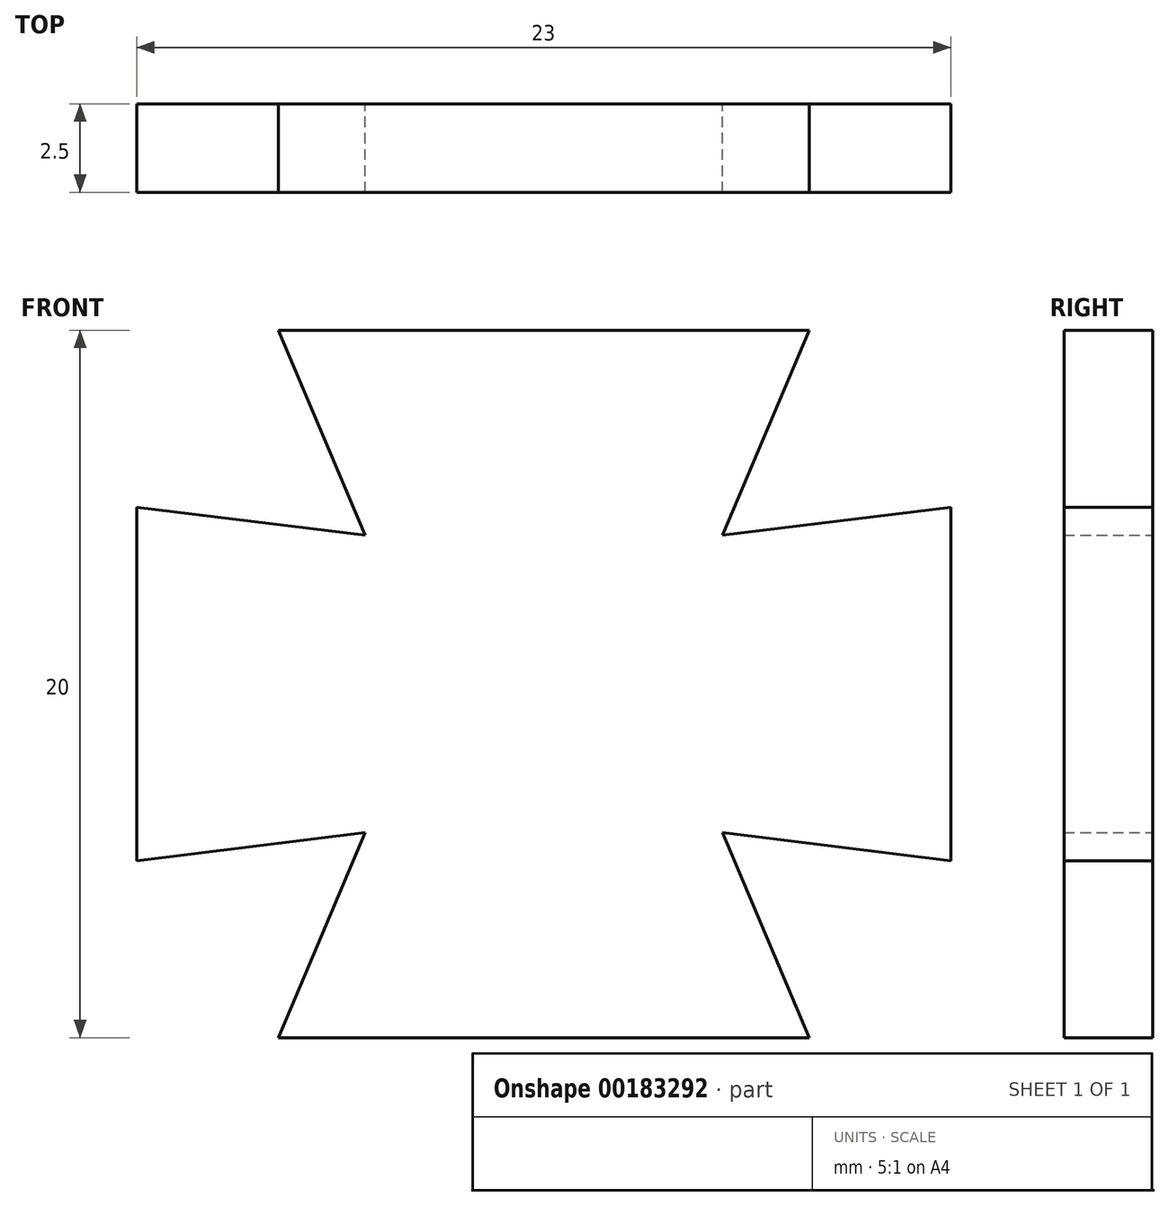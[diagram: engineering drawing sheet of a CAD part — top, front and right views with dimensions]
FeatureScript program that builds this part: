
annotation { "Feature Type Name" : "Feature", "Feature Type Description" : "" }
export const myFeature = defineFeature(function(context is Context, id is Id, definition is map)
    precondition{}
    {
        {
            var Q0;
            Q0=qCreatedBy(makeId("Front.planeOp"),FACE);
            var sketch = newSketch(context, id + "F0", { "sketchPlane" : qUnion([Q0])});
            skLineSegment(sketch, "E0", {"start": v(0, 0) * mm, "end": v(-11.5, 0) * mm});
            skLineSegment(sketch, "E1", {"start": v(0, 0) * mm, "end": v(0, 10) * mm});
            skLineSegment(sketch, "E2", {"start": v(0, 0) * mm, "end": v(0, -10) * mm});
            skLineSegment(sketch, "E3", {"start": v(0, -10) * mm, "end": v(-7.5, -10) * mm});
            skLineSegment(sketch, "E4", {"start": v(-7.5, -10) * mm, "end": v(-5.05, -4.2) * mm});
            skLineSegment(sketch, "E5", {"start": v(-5.05, -4.2) * mm, "end": v(-11.5, -5) * mm});
            skLineSegment(sketch, "E6", {"start": v(-11.5, -5) * mm, "end": v(-11.5, 0) * mm});
            skLineSegment(sketch, "E7", {"start": v(-11.5, 0) * mm, "end": v(-11.5, 5) * mm});
            skLineSegment(sketch, "E8", {"start": v(-11.5, 5) * mm, "end": v(-5.05, 4.2) * mm});
            skLineSegment(sketch, "E9", {"start": v(-5.05, 4.2) * mm, "end": v(-7.5, 10) * mm});
            skLineSegment(sketch, "E10", {"start": v(-7.5, 10) * mm, "end": v(0, 10) * mm});
            skLineSegment(sketch, "E11", {"start": v(0, 10) * mm, "end": v(0, -10) * mm});
            skLineSegment(sketch, "E12", {"start": v(0, 14.62) * mm, "end": v(0, -19.55) * mm});
            skPoint(sketch, "E12.endSnap0", {"position": v(0, -5) * mm});
            skSolve(sketch);
        }
        {
            var Q0;
            {var subQ0=sQuery(id+"F0.wireOp",EDGE,"E0");Q0=makeQuery(id+"F0.imprint","IMPRINT",FACE,{"disambiguationData":[TD([[makeQuery(id+"F0.imprint","IMPRINT",EDGE,{"derivedFrom":subQ0}),-1.0]])]});}
            var Q1;
            {var subQ1=sQuery(id+"F0.wireOp",EDGE,"E0");Q1=makeQuery(id+"F0.imprint","IMPRINT",FACE,{"disambiguationData":[TD([[makeQuery(id+"F0.imprint","IMPRINT",EDGE,{"derivedFrom":subQ1}),1.0]])]});}
            extrude(context, id + "F1", {"entities" : qUnion([Q0, Q1]), "depth" : 2.5 * mm});
        }
        {
            var Q0;
            Q0=makeQuery(id+"F1.opExtrude","SWEPT_BODY",BODY,{"disambiguationData":[OSD([sQuery(id+"F0.wireOp",EDGE,"E3"),sQuery(id+"F0.wireOp",EDGE,"E4"),sQuery(id+"F0.wireOp",EDGE,"E5"),sQuery(id+"F0.wireOp",EDGE,"E6"),sQuery(id+"F0.wireOp",EDGE,"E7"),sQuery(id+"F0.wireOp",EDGE,"E8"),sQuery(id+"F0.wireOp",EDGE,"E9"),sQuery(id+"F0.wireOp",EDGE,"E10"),sQuery(id+"F0.wireOp",EDGE,"E12")])]});
            var Q1;
            Q1=qCreatedBy(makeId("Right.planeOp"),FACE);
            mirror(context, id + "F2", {"operationType" : NewBodyOperationType.ADD, "entities" : qUnion([Q0]), "mirrorPlane" : qUnion([Q1])});
        }
    });
